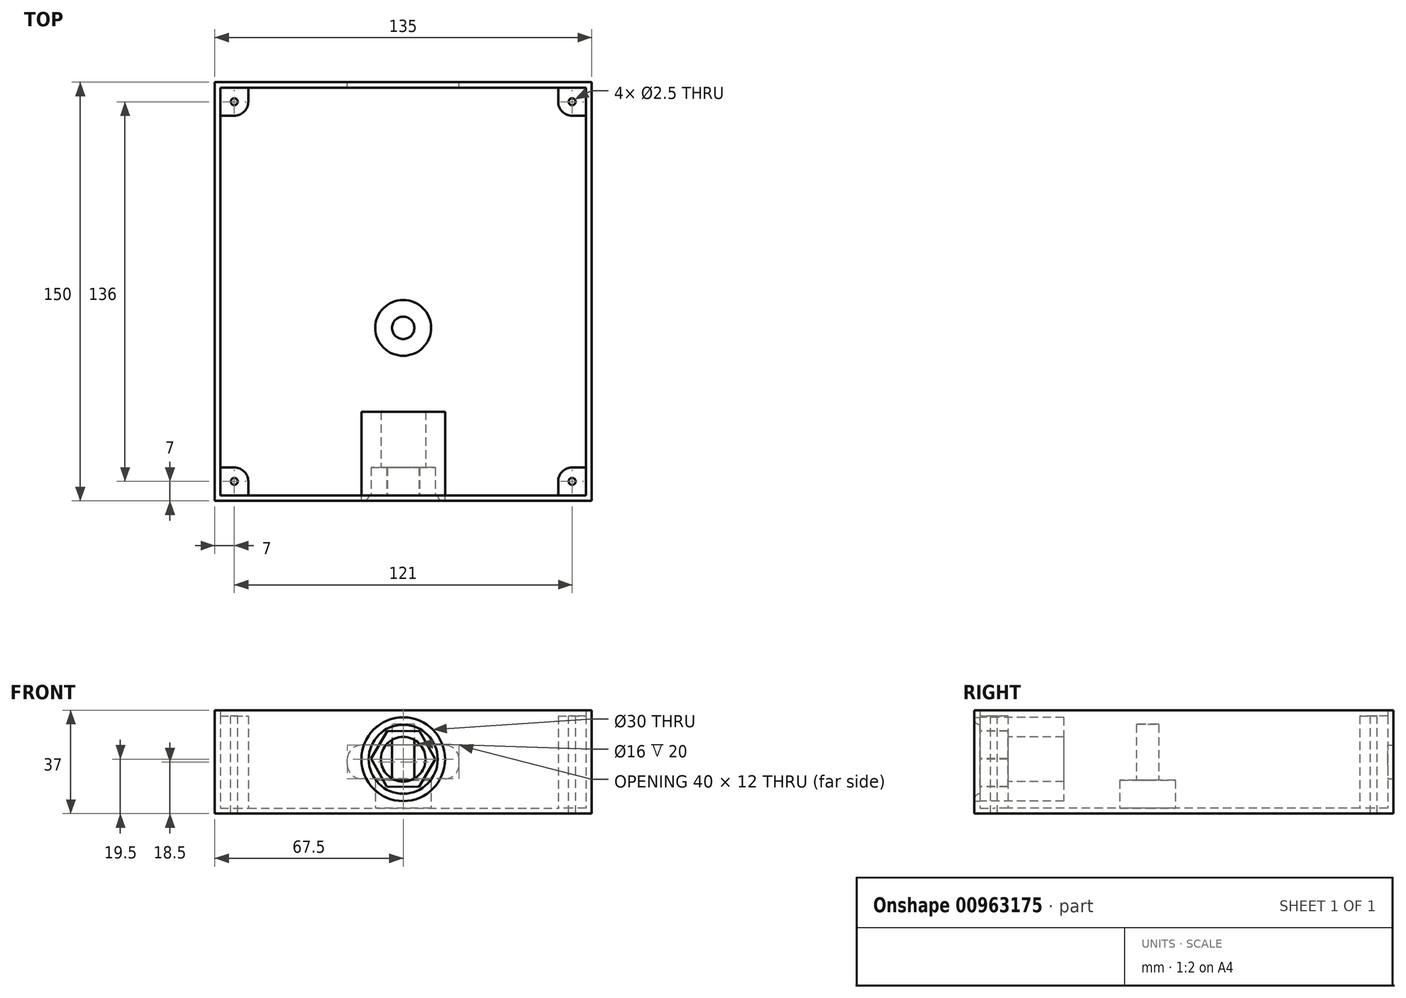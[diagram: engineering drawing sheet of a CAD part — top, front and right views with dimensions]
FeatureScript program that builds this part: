
annotation { "Feature Type Name" : "Feature", "Feature Type Description" : "" }
export const myFeature = defineFeature(function(context is Context, id is Id, definition is map)
    precondition{}
    {
        {
            var Q0;
            Q0=qCreatedBy(makeId("Top.planeOp"),FACE);
            var sketch = newSketch(context, id + "F0", { "sketchPlane" : qUnion([Q0])});
            skLineSegment(sketch, "E0.bottom", {"start": v(-67.5, -75) * mm, "end": v(67.5, -75) * mm});
            skLineSegment(sketch, "E0.top", {"start": v(-67.5, 75) * mm, "end": v(67.5, 75) * mm});
            skLineSegment(sketch, "E0.left", {"start": v(-67.5, -75) * mm, "end": v(-67.5, 75) * mm});
            skLineSegment(sketch, "E0.right", {"start": v(67.5, -75) * mm, "end": v(67.5, 75) * mm});
            skPoint(sketch, "E0.middle", {"position": v(0, 0) * mm});
            skSolve(sketch);
        }
        {
            var Q0;
            Q0=makeQuery(id+"F0.imprint","IMPRINT",FACE,{"disambiguationData":[TD([[makeQuery(id+"F0.imprint","IMPRINT",EDGE,{"derivedFrom":sQuery(id+"F0.wireOp",EDGE,"E0.bottom")}),1.0]])]});
            extrude(context, id + "F1", {"entities" : qUnion([Q0]), "depth" : 2 * mm, "offsetDistance" : 25 * mm});
        }
        {
            var Q0;
            Q0=makeQuery(id+"F1.opExtrude","CAP_FACE",FACE,{"disambiguationData":[OSD([sQuery(id+"F0.wireOp",EDGE,"E0.bottom"),sQuery(id+"F0.wireOp",EDGE,"E0.top"),sQuery(id+"F0.wireOp",EDGE,"E0.left"),sQuery(id+"F0.wireOp",EDGE,"E0.right")])],"isStart":false});
            var sketch = newSketch(context, id + "F2", { "sketchPlane" : qUnion([Q0])});
            skLineSegment(sketch, "E1.bottom", {"start": v(-67.5, 75) * mm, "end": v(67.5, 75) * mm});
            skLineSegment(sketch, "E1.top", {"start": v(-67.5, -75) * mm, "end": v(67.5, -75) * mm});
            skLineSegment(sketch, "E1.left", {"start": v(-67.5, 75) * mm, "end": v(-67.5, -75) * mm});
            skLineSegment(sketch, "E1.right", {"start": v(67.5, 75) * mm, "end": v(67.5, -75) * mm});
            skLineSegment(sketch, "E2.0", {"start": v(-65.5, 73) * mm, "end": v(-65.5, -73) * mm});
            skLineSegment(sketch, "E2.1", {"start": v(-65.5, 73) * mm, "end": v(65.5, 73) * mm});
            skLineSegment(sketch, "E2.2", {"start": v(65.5, 73) * mm, "end": v(65.5, -73) * mm});
            skLineSegment(sketch, "E2.3", {"start": v(-65.5, -73) * mm, "end": v(65.5, -73) * mm});
            skSolve(sketch);
        }
        {
            var Q0;
            Q0=makeQuery(id+"F2.imprint","IMPRINT",FACE,{"disambiguationData":[TD([[makeQuery(id+"F2.imprint","IMPRINT",EDGE,{"derivedFrom":sQuery(id+"F2.wireOp",EDGE,"E1.bottom")}),-1.0]])]});
            extrude(context, id + "F3", {"entities" : qUnion([Q0]), "operationType" : NewBodyOperationType.ADD, "depth" : 35 * mm, "offsetDistance" : 25 * mm});
        }
        {
            var Q0;
            Q0=makeQuery(id+"F1.opExtrude","CAP_FACE",FACE,{"disambiguationData":[OSD([sQuery(id+"F0.wireOp",EDGE,"E0.bottom"),sQuery(id+"F0.wireOp",EDGE,"E0.top"),sQuery(id+"F0.wireOp",EDGE,"E0.left"),sQuery(id+"F0.wireOp",EDGE,"E0.right")])],"isStart":false});
            var sketch = newSketch(context, id + "F4", { "sketchPlane" : qUnion([Q0])});
            skCircle(sketch, "E3", {"center": v(0, -13) * mm, "radius": 4 * mm});
            skSolve(sketch);
        }
        {
            var Q0;
            Q0=makeQuery(id+"F4.imprint","IMPRINT",FACE,{"disambiguationData":[TD([[makeQuery(id+"F4.imprint","IMPRINT",EDGE,{"derivedFrom":sQuery(id+"F4.wireOp",EDGE,"E3")}),1.0]])]});
            extrude(context, id + "F5", {"entities" : qUnion([Q0]), "operationType" : NewBodyOperationType.ADD, "depth" : 30 * mm, "offsetDistance" : 25 * mm});
        }
        {
            var Q0;
            Q0=makeQuery(id+"F1.opExtrude","CAP_FACE",FACE,{"disambiguationData":[OSD([sQuery(id+"F0.wireOp",EDGE,"E0.bottom"),sQuery(id+"F0.wireOp",EDGE,"E0.top"),sQuery(id+"F0.wireOp",EDGE,"E0.left"),sQuery(id+"F0.wireOp",EDGE,"E0.right")])],"isStart":false});
            var sketch = newSketch(context, id + "F6", { "sketchPlane" : qUnion([Q0])});
            skCircle(sketch, "E4", {"center": v(0, -13) * mm, "radius": 10 * mm});
            skSolve(sketch);
        }
        {
            var Q0;
            Q0=makeQuery(id+"F6.imprint","IMPRINT",FACE,{"disambiguationData":[TD([[makeQuery(id+"F6.imprint","IMPRINT",EDGE,{"derivedFrom":sQuery(id+"F6.wireOp",EDGE,"E4")}),1.0]])]});
            extrude(context, id + "F7", {"entities" : qUnion([Q0]), "operationType" : NewBodyOperationType.ADD, "depth" : 10 * mm, "offsetDistance" : 25 * mm});
        }
        {
            var Q0;
            Q0=makeQuery(id+"F3.opExtrude","SWEPT_FACE",FACE,{"disambiguationData":[OSD([sQuery(id+"F2.wireOp",EDGE,"E2.3")])]});
            var sketch = newSketch(context, id + "F8", { "sketchPlane" : qUnion([Q0])});
            skCircle(sketch, "E5", {"center": v(0, 19.5) * mm, "radius": 15 * mm});
            skPoint(sketch, "E5.centerSnap0", {"position": v(65.5, 19.5) * mm});
            skPoint(sketch, "E5.centerSnap1", {"position": v(0, 2) * mm});
            skSolve(sketch);
        }
        {
            var Q0;
            Q0=makeQuery(id+"F8.imprint","IMPRINT",FACE,{"disambiguationData":[TD([[makeQuery(id+"F8.imprint","IMPRINT",EDGE,{"derivedFrom":sQuery(id+"F8.wireOp",EDGE,"E5")}),1.0]])]});
            var sketch = newSketch(context, id + "F9", { "sketchPlane" : qUnion([Q0])});
            skCircle(sketch, "E6.cCircle", {"center": v(0, 19.62) * mm, "radius": 11.55 * mm, "construction": true});
            skLineSegment(sketch, "E6.0", {"start": v(11.55, 19.73) * mm, "end": v(5.87, 9.67) * mm});
            skLineSegment(sketch, "E6.1", {"start": v(5.87, 9.67) * mm, "end": v(-5.67, 9.56) * mm});
            skLineSegment(sketch, "E6.2", {"start": v(-5.67, 9.56) * mm, "end": v(-11.55, 19.5) * mm});
            skLineSegment(sketch, "E6.3", {"start": v(-11.55, 19.5) * mm, "end": v(-5.87, 29.56) * mm});
            skLineSegment(sketch, "E6.4", {"start": v(-5.87, 29.56) * mm, "end": v(5.67, 29.67) * mm});
            skLineSegment(sketch, "E6.5", {"start": v(5.67, 29.67) * mm, "end": v(11.55, 19.73) * mm});
            skSolve(sketch);
        }
        {
            var Q0;
            Q0=makeQuery(id+"F9.imprint","IMPRINT",FACE,{"disambiguationData":[TD([[makeQuery(id+"F9.imprint","IMPRINT",EDGE,{"derivedFrom":sQuery(id+"F9.wireOp",EDGE,"E6.0")}),1.0]])]});
            extrude(context, id + "F10", {"entities" : qUnion([Q0]), "operationType" : NewBodyOperationType.ADD, "depth" : 10 * mm, "offsetDistance" : 25 * mm});
        }
        {
            var Q0;
            Q0=makeQuery(id+"F10.opExtrude","CAP_FACE",FACE,{"disambiguationData":[OSD([sQuery(id+"F8.wireOp",EDGE,"E5"),sQuery(id+"F9.wireOp",EDGE,"E6.0"),sQuery(id+"F9.wireOp",EDGE,"E6.1"),sQuery(id+"F9.wireOp",EDGE,"E6.2"),sQuery(id+"F9.wireOp",EDGE,"E6.3"),sQuery(id+"F9.wireOp",EDGE,"E6.4"),sQuery(id+"F9.wireOp",EDGE,"E6.5")])],"isStart":false});
            extrude(context, id + "F11", {"entities" : qUnion([Q0]), "operationType" : NewBodyOperationType.ADD, "depth" : 0 * mm, "offsetDistance" : 25 * mm, "hasSecondDirection" : true, "secondDirectionOppositeDirection" : true, "secondDirectionDepth" : 12 * mm});
        }
        {
            var Q0;
            Q0=makeQuery(id+"F8.imprint","IMPRINT",FACE,{"disambiguationData":[TD([[makeQuery(id+"F8.imprint","IMPRINT",EDGE,{"derivedFrom":sQuery(id+"F8.wireOp",EDGE,"E5")}),1.0]])]});
            extrude(context, id + "F12", {"entities" : qUnion([Q0]), "operationType" : NewBodyOperationType.REMOVE, "oppositeDirection" : true, "depth" : 5 * mm, "offsetDistance" : 25 * mm});
        }
        {
            var Q0;
            Q0=makeQuery(id+"F10.opExtrude","CAP_FACE",FACE,{"disambiguationData":[OSD([sQuery(id+"F8.wireOp",EDGE,"E5"),sQuery(id+"F9.wireOp",EDGE,"E6.0"),sQuery(id+"F9.wireOp",EDGE,"E6.1"),sQuery(id+"F9.wireOp",EDGE,"E6.2"),sQuery(id+"F9.wireOp",EDGE,"E6.3"),sQuery(id+"F9.wireOp",EDGE,"E6.4"),sQuery(id+"F9.wireOp",EDGE,"E6.5")])],"isStart":false});
            var sketch = newSketch(context, id + "F13", { "sketchPlane" : qUnion([Q0])});
            skCircle(sketch, "E7", {"center": v(0, 19.5) * mm, "radius": 15 * mm});
            skCircle(sketch, "E8", {"center": v(0, 19.5) * mm, "radius": 8 * mm});
            skSolve(sketch);
        }
        {
            var Q0;
            Q0=makeQuery(id+"F13.imprint","IMPRINT",FACE,{"disambiguationData":[TD([[makeQuery(id+"F13.imprint","IMPRINT",EDGE,{"derivedFrom":sQuery(id+"F13.wireOp",EDGE,"E8")}),-1.0]])]});
            var Q1;
            Q1=makeQuery(id+"F13.imprint","IMPRINT",FACE,{"disambiguationData":[TD([[makeQuery(id+"F13.imprint","IMPRINT",EDGE,{"derivedFrom":sQuery(id+"F13.wireOp",EDGE,"E7")}),1.0]])]});
            extrude(context, id + "F14", {"entities" : qUnion([Q0, Q1]), "operationType" : NewBodyOperationType.ADD, "depth" : 20 * mm, "offsetDistance" : 25 * mm});
        }
        {
            var Q0;
            Q0=makeQuery(id+"F3.boolean.opBoolean","MERGE",FACE,{"derivedFrom":[makeQuery(id+"F1.opExtrude","SWEPT_FACE",FACE,{"disambiguationData":[OSD([sQuery(id+"F0.wireOp",EDGE,"E0.top")])]}),makeQuery(id+"F3.opExtrude","SWEPT_FACE",FACE,{"disambiguationData":[OSD([sQuery(id+"F2.wireOp",EDGE,"E1.bottom")])]})]});
            var sketch = newSketch(context, id + "F15", { "sketchPlane" : qUnion([Q0])});
            skLineSegment(sketch, "E9.bottom", {"start": v(-20, 12.5) * mm, "end": v(20, 12.5) * mm});
            skLineSegment(sketch, "E9.top", {"start": v(-20, 24.5) * mm, "end": v(20, 24.5) * mm});
            skLineSegment(sketch, "E9.left", {"start": v(-20, 12.5) * mm, "end": v(-20, 24.5) * mm});
            skLineSegment(sketch, "E9.right", {"start": v(20, 12.5) * mm, "end": v(20, 24.5) * mm});
            skPoint(sketch, "E9.middle", {"position": v(0, 18.5) * mm});
            skPoint(sketch, "E9.middle.positionSnap0", {"position": v(-67.5, 18.5) * mm});
            skPoint(sketch, "E9.centerSnap0", {"position": v(-67.5, 18.5) * mm});
            skSolve(sketch);
        }
        {
            var Q0;
            Q0=makeQuery(id+"F15.imprint","IMPRINT",FACE,{"disambiguationData":[TD([[makeQuery(id+"F15.imprint","IMPRINT",EDGE,{"derivedFrom":sQuery(id+"F15.wireOp",EDGE,"E9.bottom")}),1.0]])]});
            extrude(context, id + "F16", {"entities" : qUnion([Q0]), "operationType" : NewBodyOperationType.REMOVE, "oppositeDirection" : true, "depth" : 2 * mm, "offsetDistance" : 25 * mm});
        }
        {
            var Q0;
            {var subQ0=sQuery(id+"F15.wireOp",EDGE,"E9.bottom");var subQ1=sQuery(id+"F15.wireOp",EDGE,"E9.right");Q0=makeQuery(id+"F16.boolean.opBoolean","COPY",EDGE,{"disambiguationData":[TD([makeQuery(id+"F1.opExtrude","SWEPT_FACE",FACE,{"disambiguationData":[OSD([sQuery(id+"F0.wireOp",EDGE,"E0.top")])]})])],"derivedFrom":makeQuery(id+"F16.opExtrude","SWEPT_EDGE",EDGE,{"disambiguationData":[OSD([subQ0,subQ1])]})});}
            var Q1;
            {var subQ0=sQuery(id+"F15.wireOp",EDGE,"E9.bottom");var subQ1=sQuery(id+"F15.wireOp",EDGE,"E9.left");Q1=makeQuery(id+"F16.boolean.opBoolean","COPY",EDGE,{"disambiguationData":[TD([makeQuery(id+"F1.opExtrude","SWEPT_FACE",FACE,{"disambiguationData":[OSD([sQuery(id+"F0.wireOp",EDGE,"E0.top")])]})])],"derivedFrom":makeQuery(id+"F16.opExtrude","SWEPT_EDGE",EDGE,{"disambiguationData":[OSD([subQ0,subQ1])]})});}
            var Q2;
            {var subQ0=sQuery(id+"F15.wireOp",EDGE,"E9.top");var subQ1=sQuery(id+"F15.wireOp",EDGE,"E9.right");Q2=makeQuery(id+"F16.boolean.opBoolean","COPY",EDGE,{"disambiguationData":[TD([makeQuery(id+"F1.opExtrude","SWEPT_FACE",FACE,{"disambiguationData":[OSD([sQuery(id+"F0.wireOp",EDGE,"E0.top")])]})])],"derivedFrom":makeQuery(id+"F16.opExtrude","SWEPT_EDGE",EDGE,{"disambiguationData":[OSD([subQ0,subQ1])]})});}
            var Q3;
            {var subQ0=sQuery(id+"F15.wireOp",EDGE,"E9.top");var subQ1=sQuery(id+"F15.wireOp",EDGE,"E9.left");Q3=makeQuery(id+"F16.boolean.opBoolean","COPY",EDGE,{"disambiguationData":[TD([makeQuery(id+"F1.opExtrude","SWEPT_FACE",FACE,{"disambiguationData":[OSD([sQuery(id+"F0.wireOp",EDGE,"E0.top")])]})])],"derivedFrom":makeQuery(id+"F16.opExtrude","SWEPT_EDGE",EDGE,{"disambiguationData":[OSD([subQ0,subQ1])]})});}
            fillet(context, id + "F17", {"entities" : qUnion([Q0, Q1, Q2, Q3]), "radius" : 5 * mm, "tangentPropagation" : true, "allowEdgeOverflow" : false});
        }
        {
            var Q0;
            Q0=makeQuery(id+"F1.opExtrude","CAP_FACE",FACE,{"disambiguationData":[OSD([sQuery(id+"F0.wireOp",EDGE,"E0.bottom"),sQuery(id+"F0.wireOp",EDGE,"E0.top"),sQuery(id+"F0.wireOp",EDGE,"E0.left"),sQuery(id+"F0.wireOp",EDGE,"E0.right")])],"isStart":false});
            var sketch = newSketch(context, id + "F18", { "sketchPlane" : qUnion([Q0])});
            skLineSegment(sketch, "E10.bottom", {"start": v(-65.5, 73) * mm, "end": v(-55.5, 73) * mm});
            skLineSegment(sketch, "E10.top", {"start": v(-65.5, 63) * mm, "end": v(-55.5, 63) * mm});
            skLineSegment(sketch, "E10.left", {"start": v(-65.5, 73) * mm, "end": v(-65.5, 63) * mm});
            skLineSegment(sketch, "E10.right", {"start": v(-55.5, 73) * mm, "end": v(-55.5, 63) * mm});
            skLineSegment(sketch, "E11.bottom", {"start": v(65.5, 73) * mm, "end": v(55.5, 73) * mm});
            skLineSegment(sketch, "E11.top", {"start": v(65.5, 63) * mm, "end": v(55.5, 63) * mm});
            skLineSegment(sketch, "E11.left", {"start": v(65.5, 73) * mm, "end": v(65.5, 63) * mm});
            skLineSegment(sketch, "E11.right", {"start": v(55.5, 73) * mm, "end": v(55.5, 63) * mm});
            skLineSegment(sketch, "E12.bottom", {"start": v(-65.5, -73) * mm, "end": v(-55.5, -73) * mm});
            skLineSegment(sketch, "E12.top", {"start": v(-65.5, -63) * mm, "end": v(-55.5, -63) * mm});
            skLineSegment(sketch, "E12.left", {"start": v(-65.5, -73) * mm, "end": v(-65.5, -63) * mm});
            skLineSegment(sketch, "E12.right", {"start": v(-55.5, -73) * mm, "end": v(-55.5, -63) * mm});
            skLineSegment(sketch, "E13.bottom", {"start": v(65.5, -73) * mm, "end": v(55.5, -73) * mm});
            skLineSegment(sketch, "E13.top", {"start": v(65.5, -63) * mm, "end": v(55.5, -63) * mm});
            skLineSegment(sketch, "E13.left", {"start": v(65.5, -73) * mm, "end": v(65.5, -63) * mm});
            skLineSegment(sketch, "E13.right", {"start": v(55.5, -73) * mm, "end": v(55.5, -63) * mm});
            skSolve(sketch);
        }
        {
            var Q0;
            Q0=makeQuery(id+"F18.imprint","IMPRINT",FACE,{"disambiguationData":[TD([[makeQuery(id+"F18.imprint","IMPRINT",EDGE,{"derivedFrom":sQuery(id+"F18.wireOp",EDGE,"E10.bottom")}),-1.0]])]});
            var Q1;
            Q1=makeQuery(id+"F18.imprint","IMPRINT",FACE,{"disambiguationData":[TD([[makeQuery(id+"F18.imprint","IMPRINT",EDGE,{"derivedFrom":sQuery(id+"F18.wireOp",EDGE,"E11.bottom")}),-1.0]])]});
            var Q2;
            Q2=makeQuery(id+"F18.imprint","IMPRINT",FACE,{"disambiguationData":[TD([[makeQuery(id+"F18.imprint","IMPRINT",EDGE,{"derivedFrom":sQuery(id+"F18.wireOp",EDGE,"E13.bottom")}),1.0]])]});
            var Q3;
            Q3=makeQuery(id+"F18.imprint","IMPRINT",FACE,{"disambiguationData":[TD([[makeQuery(id+"F18.imprint","IMPRINT",EDGE,{"derivedFrom":sQuery(id+"F18.wireOp",EDGE,"E12.bottom")}),1.0]])]});
            extrude(context, id + "F19", {"entities" : qUnion([Q0, Q1, Q2, Q3]), "operationType" : NewBodyOperationType.ADD, "depth" : 33 * mm, "offsetDistance" : 25 * mm});
        }
        {
            var Q0;
            Q0=makeQuery(id+"F19.opExtrude","CAP_FACE",FACE,{"disambiguationData":[OSD([sQuery(id+"F18.wireOp",EDGE,"E10.bottom"),sQuery(id+"F18.wireOp",EDGE,"E10.top"),sQuery(id+"F18.wireOp",EDGE,"E10.left"),sQuery(id+"F18.wireOp",EDGE,"E10.right")])],"isStart":false});
            var sketch = newSketch(context, id + "F20", { "sketchPlane" : qUnion([Q0])});
            skCircle(sketch, "E14", {"center": v(-60.5, 68) * mm, "radius": 1.25 * mm});
            skCircle(sketch, "E15", {"center": v(60.5, 68) * mm, "radius": 1.25 * mm});
            skCircle(sketch, "E16", {"center": v(60.5, -68) * mm, "radius": 1.25 * mm});
            skCircle(sketch, "E17", {"center": v(-60.5, -68) * mm, "radius": 1.25 * mm});
            skSolve(sketch);
        }
        {
            var Q0;
            Q0=makeQuery(id+"F20.imprint","IMPRINT",FACE,{"disambiguationData":[TD([[makeQuery(id+"F20.imprint","IMPRINT",EDGE,{"derivedFrom":sQuery(id+"F20.wireOp",EDGE,"E14")}),1.0]])]});
            var Q1;
            Q1=makeQuery(id+"F20.imprint","IMPRINT",FACE,{"disambiguationData":[TD([[makeQuery(id+"F20.imprint","IMPRINT",EDGE,{"derivedFrom":sQuery(id+"F20.wireOp",EDGE,"E15")}),1.0]])]});
            var Q2;
            Q2=makeQuery(id+"F20.imprint","IMPRINT",FACE,{"disambiguationData":[TD([[makeQuery(id+"F20.imprint","IMPRINT",EDGE,{"derivedFrom":sQuery(id+"F20.wireOp",EDGE,"E16")}),1.0]])]});
            var Q3;
            Q3=makeQuery(id+"F20.imprint","IMPRINT",FACE,{"disambiguationData":[TD([[makeQuery(id+"F20.imprint","IMPRINT",EDGE,{"derivedFrom":sQuery(id+"F20.wireOp",EDGE,"E17")}),1.0]])]});
            extrude(context, id + "F21", {"entities" : qUnion([Q0, Q1, Q2, Q3]), "operationType" : NewBodyOperationType.REMOVE, "endBound" : BoundingType.THROUGH_ALL, "oppositeDirection" : true, "depth" : 25 * mm, "offsetDistance" : 25 * mm});
        }
        {
            var Q0;
            Q0=makeQuery(id+"F19.opExtrude","SWEPT_EDGE",EDGE,{"disambiguationData":[OSD([sQuery(id+"F2.wireOp",EDGE,"E2.1"),sQuery(id+"F18.wireOp",EDGE,"E10.bottom"),sQuery(id+"F18.wireOp",EDGE,"E10.right")])]});
            var Q1;
            Q1=makeQuery(id+"F19.opExtrude","SWEPT_EDGE",EDGE,{"disambiguationData":[OSD([sQuery(id+"F18.wireOp",EDGE,"E10.top"),sQuery(id+"F18.wireOp",EDGE,"E10.right")])]});
            var Q2;
            Q2=makeQuery(id+"F19.opExtrude","SWEPT_EDGE",EDGE,{"disambiguationData":[OSD([sQuery(id+"F2.wireOp",EDGE,"E2.0"),sQuery(id+"F18.wireOp",EDGE,"E10.top"),sQuery(id+"F18.wireOp",EDGE,"E10.left")])]});
            var Q3;
            Q3=makeQuery(id+"F19.opExtrude","SWEPT_EDGE",EDGE,{"disambiguationData":[OSD([sQuery(id+"F2.wireOp",EDGE,"E2.1"),sQuery(id+"F18.wireOp",EDGE,"E11.bottom"),sQuery(id+"F18.wireOp",EDGE,"E11.right")])]});
            var Q4;
            Q4=makeQuery(id+"F19.opExtrude","SWEPT_EDGE",EDGE,{"disambiguationData":[OSD([sQuery(id+"F18.wireOp",EDGE,"E11.top"),sQuery(id+"F18.wireOp",EDGE,"E11.right")])]});
            var Q5;
            Q5=makeQuery(id+"F19.opExtrude","SWEPT_EDGE",EDGE,{"disambiguationData":[OSD([sQuery(id+"F2.wireOp",EDGE,"E2.2"),sQuery(id+"F18.wireOp",EDGE,"E11.top"),sQuery(id+"F18.wireOp",EDGE,"E11.left")])]});
            var Q6;
            Q6=makeQuery(id+"F19.opExtrude","SWEPT_EDGE",EDGE,{"disambiguationData":[OSD([sQuery(id+"F2.wireOp",EDGE,"E2.2"),sQuery(id+"F18.wireOp",EDGE,"E13.top"),sQuery(id+"F18.wireOp",EDGE,"E13.left")])]});
            var Q7;
            Q7=makeQuery(id+"F19.opExtrude","SWEPT_EDGE",EDGE,{"disambiguationData":[OSD([sQuery(id+"F18.wireOp",EDGE,"E13.top"),sQuery(id+"F18.wireOp",EDGE,"E13.right")])]});
            var Q8;
            Q8=makeQuery(id+"F19.opExtrude","SWEPT_EDGE",EDGE,{"disambiguationData":[OSD([sQuery(id+"F2.wireOp",EDGE,"E2.3"),sQuery(id+"F18.wireOp",EDGE,"E13.bottom"),sQuery(id+"F18.wireOp",EDGE,"E13.right")])]});
            var Q9;
            Q9=makeQuery(id+"F19.opExtrude","SWEPT_EDGE",EDGE,{"disambiguationData":[OSD([sQuery(id+"F2.wireOp",EDGE,"E2.0"),sQuery(id+"F18.wireOp",EDGE,"E12.top"),sQuery(id+"F18.wireOp",EDGE,"E12.left")])]});
            var Q10;
            Q10=makeQuery(id+"F19.opExtrude","SWEPT_EDGE",EDGE,{"disambiguationData":[OSD([sQuery(id+"F18.wireOp",EDGE,"E12.top"),sQuery(id+"F18.wireOp",EDGE,"E12.right")])]});
            var Q11;
            Q11=makeQuery(id+"F19.opExtrude","SWEPT_EDGE",EDGE,{"disambiguationData":[OSD([sQuery(id+"F2.wireOp",EDGE,"E2.3"),sQuery(id+"F18.wireOp",EDGE,"E12.bottom"),sQuery(id+"F18.wireOp",EDGE,"E12.right")])]});
            fillet(context, id + "F22", {"entities" : qUnion([Q0, Q1, Q2, Q3, Q4, Q5, Q6, Q7, Q8, Q9, Q10, Q11]), "radius" : 5 * mm, "tangentPropagation" : true, "allowEdgeOverflow" : false});
        }
        {
            var Q0;
            Q0=makeQuery(id+"F8.imprint","IMPRINT",FACE,{"disambiguationData":[TD([[makeQuery(id+"F8.imprint","IMPRINT",EDGE,{"derivedFrom":sQuery(id+"F8.wireOp",EDGE,"E5")}),1.0]])]});
            var sketch = newSketch(context, id + "F23", { "sketchPlane" : qUnion([Q0])});
            skCircle(sketch, "E18", {"center": v(0, 19.48) * mm, "radius": 12.36 * mm});
            skCircle(sketch, "E19", {"center": v(0, 19.48) * mm, "radius": 16.15 * mm});
            skCircle(sketch, "E20", {"center": v(0, 19.48) * mm, "radius": 15 * mm});
            skSolve(sketch);
        }
        {
            var Q0;
            Q0=makeQuery(id+"F23.imprint","IMPRINT",FACE,{"disambiguationData":[TD([[makeQuery(id+"F23.imprint","IMPRINT",EDGE,{"derivedFrom":sQuery(id+"F23.wireOp",EDGE,"E18")}),-1.0]])]});
            extrude(context, id + "F24", {"entities" : qUnion([Q0]), "oppositeDirection" : true, "depth" : 2 * mm, "offsetDistance" : 25 * mm});
        }
        {
            var Q0;
            Q0=makeQuery(id+"F24.opExtrude","CAP_EDGE",EDGE,{"disambiguationData":[OSD([sQuery(id+"F23.wireOp",EDGE,"E18")])],"isStart":false});
            fillet(context, id + "F25", {"entities" : qUnion([Q0]), "radius" : 2 * mm, "tangentPropagation" : true, "allowEdgeOverflow" : false});
        }
    });
